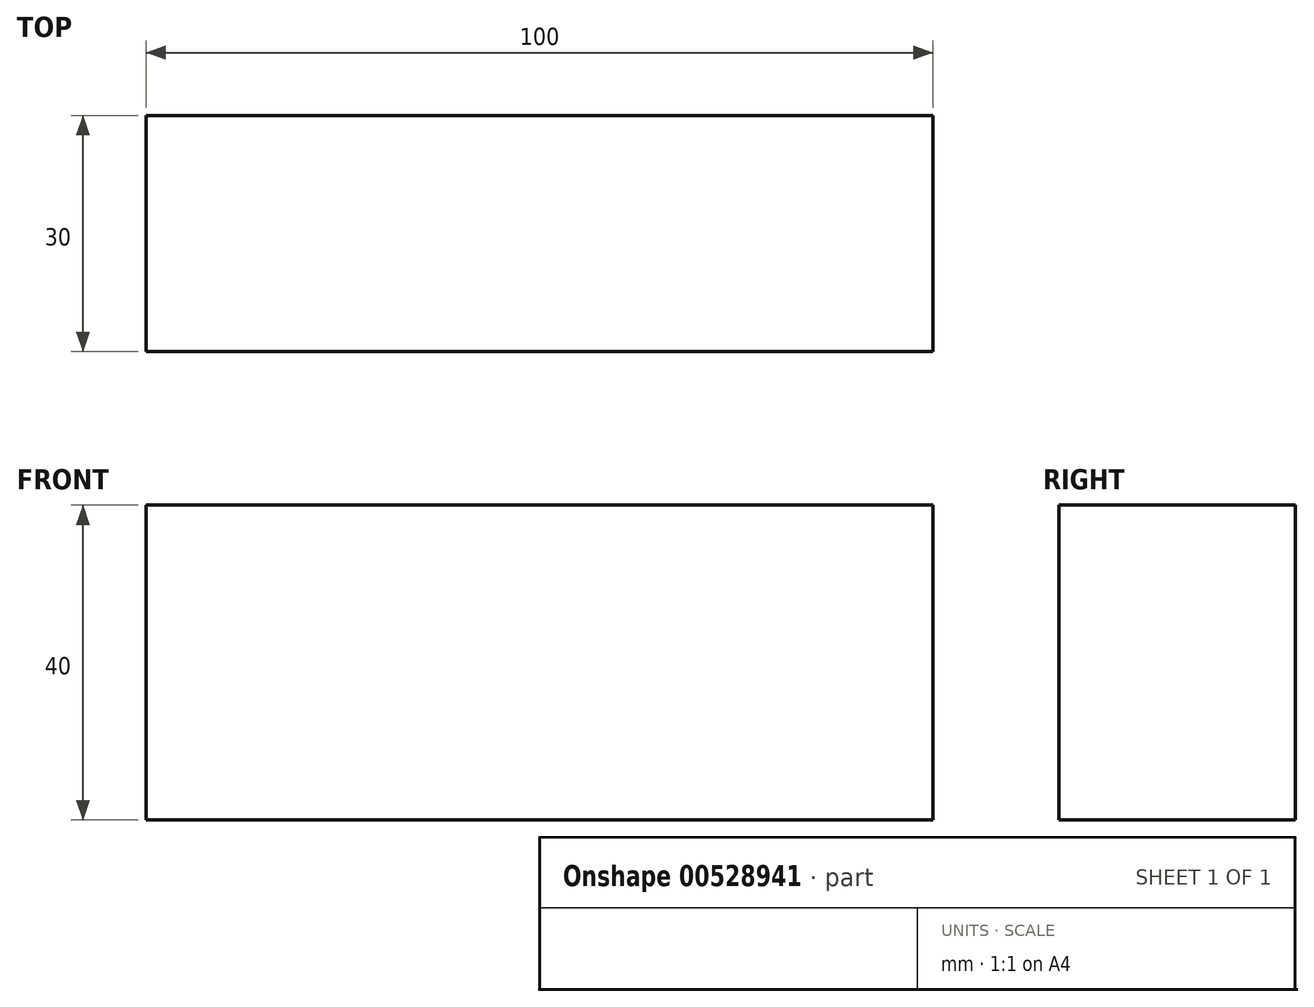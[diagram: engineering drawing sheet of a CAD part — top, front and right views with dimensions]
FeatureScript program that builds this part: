
annotation { "Feature Type Name" : "Feature", "Feature Type Description" : "" }
export const myFeature = defineFeature(function(context is Context, id is Id, definition is map)
    precondition{}
    {
        {
            var Q0;
            Q0=qCreatedBy(makeId("Top.planeOp"),FACE);
            var sketch = newSketch(context, id + "F0", { "sketchPlane" : qUnion([Q0])});
            skLineSegment(sketch, "E0.bottom", {"start": v(50, -15) * mm, "end": v(-50, -15) * mm});
            skLineSegment(sketch, "E0.top", {"start": v(50, 15) * mm, "end": v(-50, 15) * mm});
            skLineSegment(sketch, "E0.left", {"start": v(50, -15) * mm, "end": v(50, 15) * mm});
            skLineSegment(sketch, "E0.right", {"start": v(-50, -15) * mm, "end": v(-50, 15) * mm});
            skPoint(sketch, "E0.middle", {"position": v(0, 0) * mm});
            skSolve(sketch);
        }
        {
            var Q0;
            Q0=makeQuery(id+"F0.imprint","IMPRINT",FACE,{"disambiguationData":[TD([[makeQuery(id+"F0.imprint","IMPRINT",EDGE,{"derivedFrom":sQuery(id+"F0.wireOp",EDGE,"E0.bottom")}),-1.0]])]});
            extrude(context, id + "F1", {"entities" : qUnion([Q0]), "depth" : 40 * mm, "offsetDistance" : 25 * mm});
        }
    });
